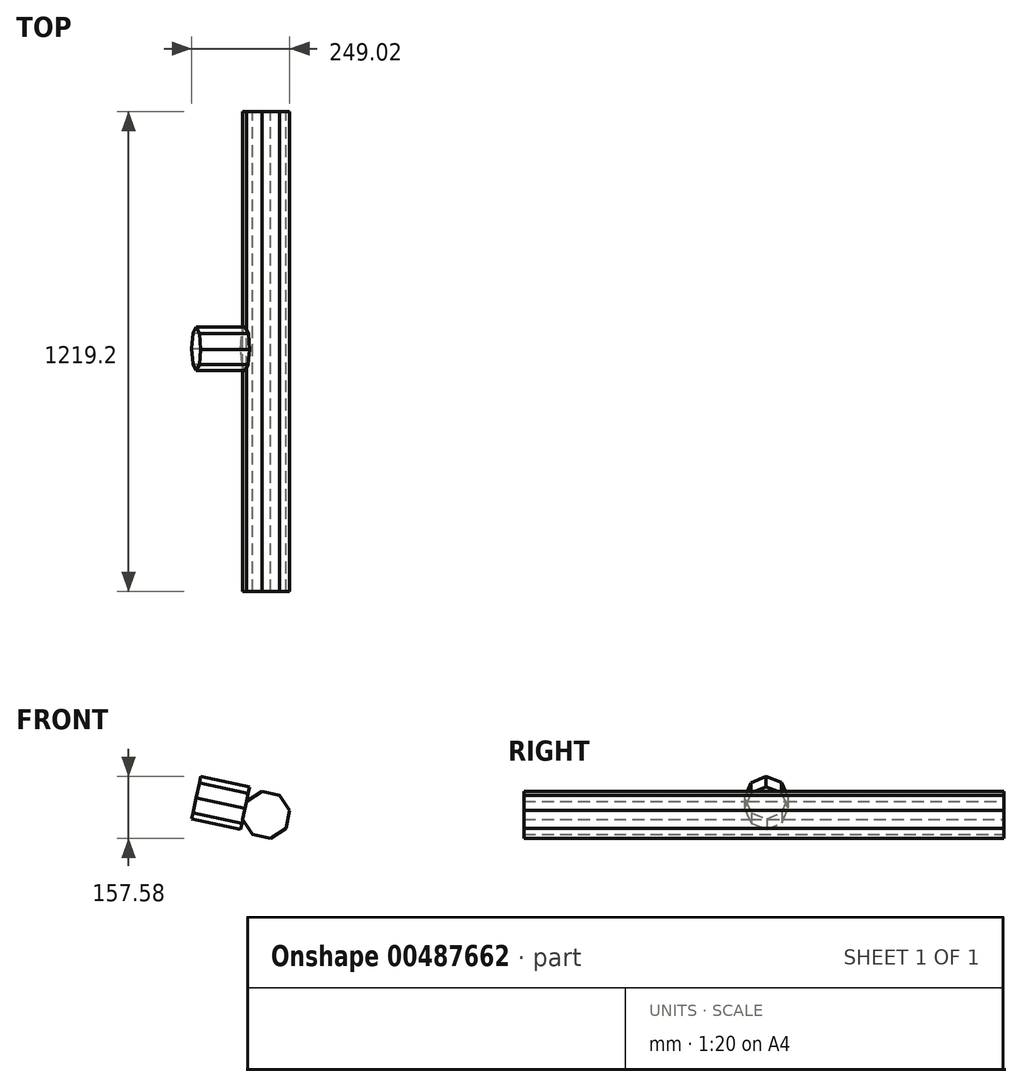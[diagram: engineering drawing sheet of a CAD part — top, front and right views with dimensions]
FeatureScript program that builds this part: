
annotation { "Feature Type Name" : "Feature", "Feature Type Description" : "" }
export const myFeature = defineFeature(function(context is Context, id is Id, definition is map)
    precondition{}
    {
        {
            var Q0;
            Q0=qCreatedBy(makeId("Front.planeOp"),FACE);
            var sketch = newSketch(context, id + "F0", { "sketchPlane" : qUnion([Q0])});
            skCircle(sketch, "E0.cCircle", {"center": v(0, 0) * mm, "radius": 56.07 * mm, "construction": true});
            skLineSegment(sketch, "E0.0", {"start": v(-59.67, -11.04) * mm, "end": v(-50, 34.39) * mm});
            skLineSegment(sketch, "E0.1", {"start": v(-50, 34.39) * mm, "end": v(-11.04, 59.67) * mm});
            skLineSegment(sketch, "E0.2", {"start": v(-11.04, 59.67) * mm, "end": v(34.39, 50) * mm});
            skLineSegment(sketch, "E0.3", {"start": v(34.39, 50) * mm, "end": v(59.67, 11.04) * mm});
            skLineSegment(sketch, "E0.4", {"start": v(59.67, 11.04) * mm, "end": v(50, -34.39) * mm});
            skLineSegment(sketch, "E0.5", {"start": v(50, -34.39) * mm, "end": v(11.04, -59.67) * mm});
            skLineSegment(sketch, "E0.6", {"start": v(11.04, -59.67) * mm, "end": v(-34.39, -50) * mm});
            skLineSegment(sketch, "E0.7", {"start": v(-34.39, -50) * mm, "end": v(-59.67, -11.04) * mm});
            skPoint(sketch, "E0.0.midPoint", {"position": v(-54.84, 11.67) * mm});
            skSolve(sketch);
        }
        {
            var Q0;
            Q0=makeQuery(id+"F0.imprint","IMPRINT",FACE,{"disambiguationData":[TD([[makeQuery(id+"F0.imprint","IMPRINT",EDGE,{"derivedFrom":sQuery(id+"F0.wireOp",EDGE,"E0.0")}),-1.0]])]});
            extrude(context, id + "F1", {"entities" : qUnion([Q0]), "depth" : 1219.2 * mm});
        }
        {
            var Q0;
            Q0=makeQuery(id+"F1.opExtrude","SWEPT_FACE",FACE,{"disambiguationData":[OSD([sQuery(id+"F0.wireOp",EDGE,"E0.0")])]});
            var sketch = newSketch(context, id + "F2", { "sketchPlane" : qUnion([Q0])});
            skCircle(sketch, "E1.cCircle", {"center": v(603, 5.84) * mm, "radius": 51.1 * mm, "construction": true});
            skLineSegment(sketch, "E1.0", {"start": v(658.3, 4.83) * mm, "end": v(641.4, -33.98) * mm});
            skLineSegment(sketch, "E1.1", {"start": v(641.4, -33.98) * mm, "end": v(602, -49.47) * mm});
            skLineSegment(sketch, "E1.2", {"start": v(602, -49.47) * mm, "end": v(563.19, -32.56) * mm});
            skLineSegment(sketch, "E1.3", {"start": v(563.19, -32.56) * mm, "end": v(547.7, 6.84) * mm});
            skLineSegment(sketch, "E1.4", {"start": v(547.7, 6.84) * mm, "end": v(564.61, 45.65) * mm});
            skLineSegment(sketch, "E1.5", {"start": v(564.61, 45.65) * mm, "end": v(604.01, 61.14) * mm});
            skLineSegment(sketch, "E1.6", {"start": v(604.01, 61.14) * mm, "end": v(642.82, 44.23) * mm});
            skLineSegment(sketch, "E1.7", {"start": v(642.82, 44.23) * mm, "end": v(658.3, 4.83) * mm});
            skPoint(sketch, "E1.0.midPoint", {"position": v(649.85, -14.57) * mm});
            skSolve(sketch);
        }
        {
            var Q0;
            {var subQ0=sQuery(id+"F2.wireOp",EDGE,"E1.7");var subQ1=sQuery(id+"F2.wireOp",EDGE,"E1.0");var subQ2=makeQuery(id+"F2.imprint","INTERSECT",VERTEX,{"derivedFrom":[subQ1,subQ0]});Q0=makeQuery(id+"F2.imprint","IMPRINT",FACE,{"disambiguationData":[TD([[makeQuery(id+"F2.imprint","IMPRINT",EDGE,{"disambiguationData":[TD([[subQ2,-1.0]])],"derivedFrom":subQ1}),-1.0]])]});}
            var Q1;
            {var subQ4=sQuery(id+"F2.wireOp",EDGE,"E1.5");Q1=makeQuery(id+"F2.imprint","IMPRINT",FACE,{"disambiguationData":[TD([[makeQuery(id+"F2.imprint","IMPRINT",EDGE,{"derivedFrom":subQ4}),-1.0]])]});}
            var Q2;
            {var subQ4=sQuery(id+"F2.wireOp",EDGE,"E1.1");Q2=makeQuery(id+"F2.imprint","IMPRINT",FACE,{"disambiguationData":[TD([[makeQuery(id+"F2.imprint","IMPRINT",EDGE,{"derivedFrom":subQ4}),-1.0]])]});}
            extrude(context, id + "F3", {"entities" : qUnion([Q0, Q1, Q2]), "operationType" : NewBodyOperationType.ADD, "depth" : 127 * mm});
        }
    });
